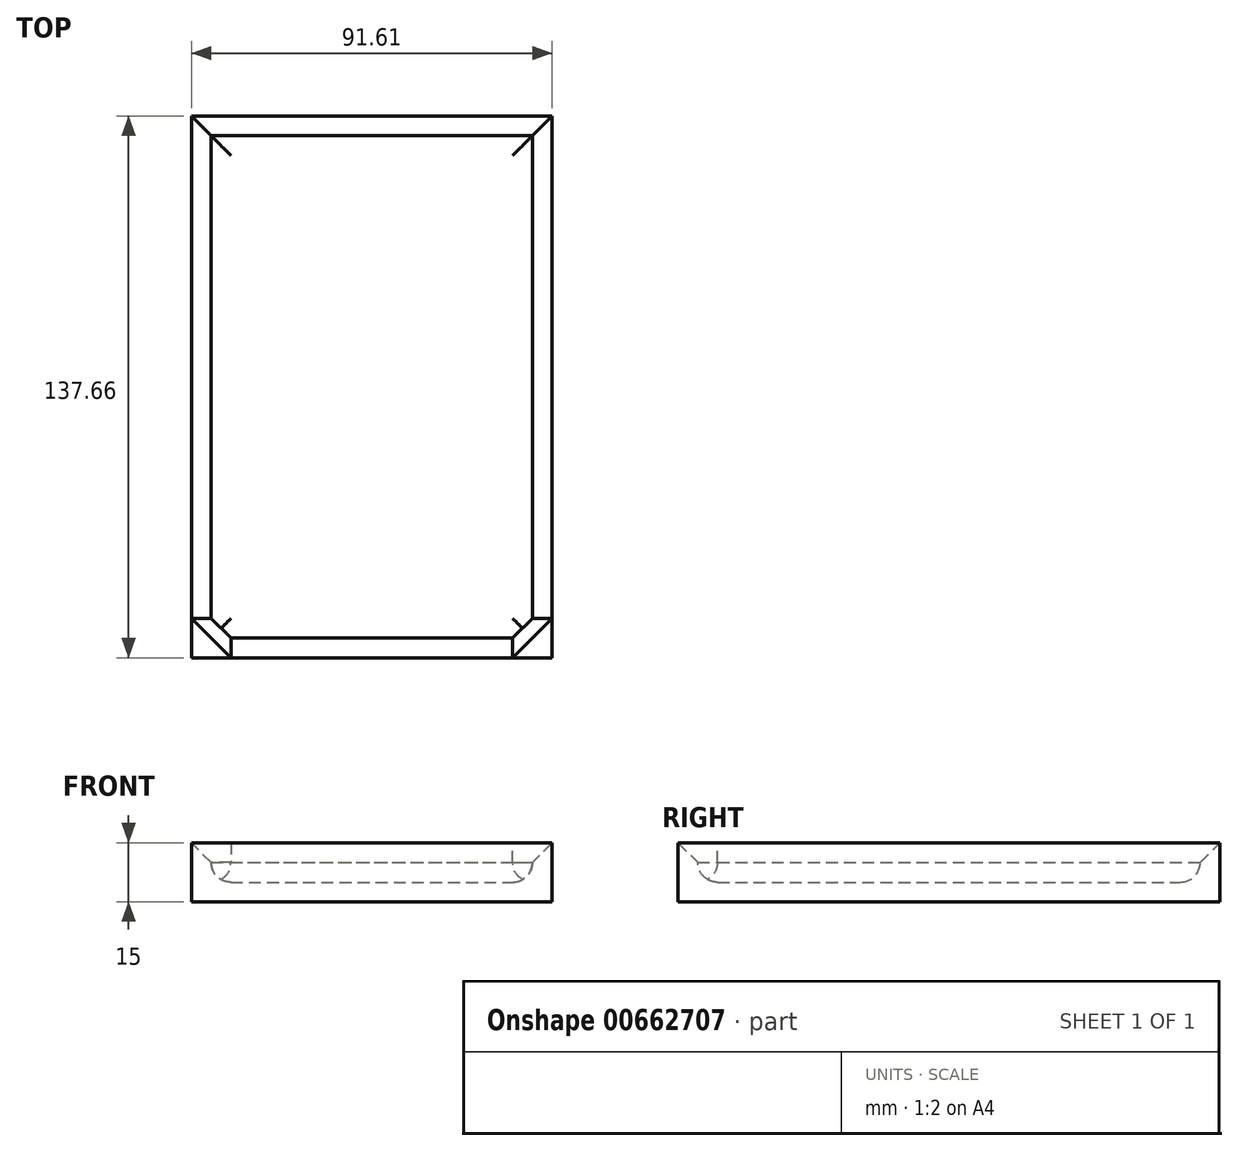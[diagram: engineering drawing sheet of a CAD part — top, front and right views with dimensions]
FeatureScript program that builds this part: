
annotation { "Feature Type Name" : "Feature", "Feature Type Description" : "" }
export const myFeature = defineFeature(function(context is Context, id is Id, definition is map)
    precondition{}
    {
        {
            var Q0;
            Q0=qCreatedBy(makeId("Top.planeOp"),FACE);
            var sketch = newSketch(context, id + "F0", { "sketchPlane" : qUnion([Q0])});
            skLineSegment(sketch, "E0.bottom", {"start": v(-47.72, -56.7) * mm, "end": v(33.89, -56.7) * mm});
            skLineSegment(sketch, "E0.top", {"start": v(-47.72, 70.96) * mm, "end": v(33.89, 70.96) * mm});
            skLineSegment(sketch, "E0.left", {"start": v(-47.72, -56.7) * mm, "end": v(-47.72, 70.96) * mm});
            skLineSegment(sketch, "E0.right", {"start": v(33.89, -56.7) * mm, "end": v(33.89, 70.96) * mm});
            skLineSegment(sketch, "E1.0", {"start": v(-52.72, 75.96) * mm, "end": v(38.89, 75.96) * mm});
            skLineSegment(sketch, "E1.1", {"start": v(-52.72, -61.7) * mm, "end": v(-52.72, 75.96) * mm});
            skLineSegment(sketch, "E1.2", {"start": v(-52.72, -61.7) * mm, "end": v(38.89, -61.7) * mm});
            skLineSegment(sketch, "E1.3", {"start": v(38.89, -61.7) * mm, "end": v(38.89, 75.96) * mm});
            skSolve(sketch);
        }
        {
            var Q0;
            Q0=makeQuery(id+"F0.imprint","IMPRINT",FACE,{"disambiguationData":[TD([[makeQuery(id+"F0.imprint","IMPRINT",EDGE,{"derivedFrom":sQuery(id+"F0.wireOp",EDGE,"E0.bottom")}),-1.0]])]});
            extrude(context, id + "F1", {"entities" : qUnion([Q0]), "depth" : 15 * mm, "offsetDistance" : 25 * mm});
        }
        {
            var Q0;
            Q0=makeQuery(id+"F0.imprint","IMPRINT",FACE,{"disambiguationData":[TD([[makeQuery(id+"F0.imprint","IMPRINT",EDGE,{"derivedFrom":sQuery(id+"F0.wireOp",EDGE,"E0.bottom")}),1.0]])]});
            extrude(context, id + "F2", {"entities" : qUnion([Q0]), "operationType" : NewBodyOperationType.ADD, "depth" : 5 * mm, "offsetDistance" : 25 * mm});
        }
        {
            var Q0;
            Q0=makeQuery(id+"F2.opExtrude","CAP_FACE",FACE,{"disambiguationData":[OSD([sQuery(id+"F0.wireOp",EDGE,"E0.bottom"),sQuery(id+"F0.wireOp",EDGE,"E0.top"),sQuery(id+"F0.wireOp",EDGE,"E0.left"),sQuery(id+"F0.wireOp",EDGE,"E0.right")])],"isStart":false});
            fillet(context, id + "F3", {"entities" : qUnion([Q0]), "radius" : 5 * mm, "tangentPropagation" : true, "allowEdgeOverflow" : false});
        }
        {
            var Q0;
            Q0=makeQuery(id+"F1.opExtrude","CAP_EDGE",EDGE,{"disambiguationData":[OSD([sQuery(id+"F0.wireOp",EDGE,"E0.left")])],"isStart":false});
            var Q1;
            Q1=makeQuery(id+"F1.opExtrude","SWEPT_FACE",FACE,{"disambiguationData":[OSD([sQuery(id+"F0.wireOp",EDGE,"E0.bottom")])]});
            var Q2;
            Q2=makeQuery(id+"F1.opExtrude","CAP_EDGE",EDGE,{"disambiguationData":[OSD([sQuery(id+"F0.wireOp",EDGE,"E0.top")])],"isStart":false});
            chamfer(context, id + "F4", {"entities" : qUnion([Q0, Q1, Q2]), "width" : 5 * mm, "tangentPropagation" : true});
        }
    });
